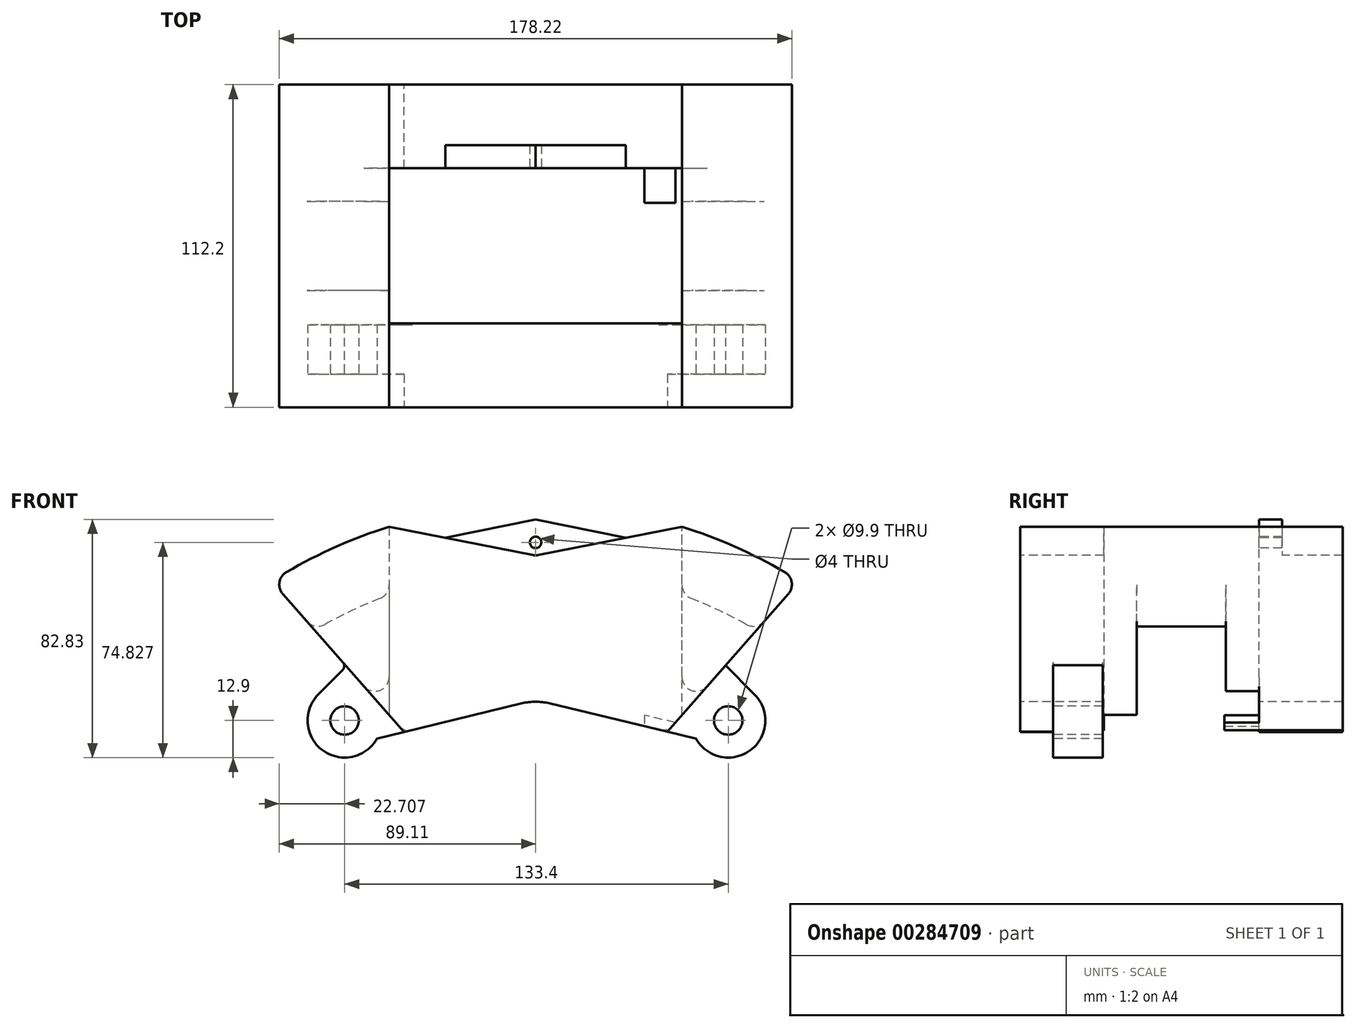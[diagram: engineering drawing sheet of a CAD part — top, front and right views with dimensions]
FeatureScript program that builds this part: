
annotation { "Feature Type Name" : "Feature", "Feature Type Description" : "" }
export const myFeature = defineFeature(function(context is Context, id is Id, definition is map)
    precondition{}
    {
        {
            var Q0;
            Q0=qCreatedBy(makeId("Front.planeOp"),FACE);
            var sketch = newSketch(context, id + "F0", { "sketchPlane" : qUnion([Q0])});
            skCircle(sketch, "E0", {"center": v(0, 0) * mm, "radius": 117.6 * mm, "construction": true});
            skPoint(sketch, "E1", {"position": v(67, 96.65) * mm});
            skLineSegment(sketch, "E2", {"start": v(67, 96.65) * mm, "end": v(-66.4, 96.65) * mm});
            skCircle(sketch, "E3", {"center": v(0, 0) * mm, "radius": 171.7 * mm, "construction": true});
            skCircle(sketch, "E4", {"center": v(67, 96.65) * mm, "radius": 4.95 * mm});
            skCircle(sketch, "E5", {"center": v(-66.4, 96.65) * mm, "radius": 4.95 * mm});
            skCircle(sketch, "E6", {"center": v(67, 96.65) * mm, "radius": 12.9 * mm});
            skCircle(sketch, "E7", {"center": v(-66.4, 96.65) * mm, "radius": 12.9 * mm});
            skPoint(sketch, "E8", {"position": v(-66.4, 83.75) * mm});
            skPoint(sketch, "E9", {"position": v(0, 83.75) * mm});
            skPoint(sketch, "E10", {"position": v(0, 103.75) * mm});
            skPoint(sketch, "E11", {"position": v(67, 83.75) * mm});
            skArc(sketch, "E12", {"start": v(55.76, 90.32) * mm, "mid": v(0.3, 103.75) * mm, "end": v(-55.16, 90.32) * mm});
            skPoint(sketch, "E13", {"position": v(0, 171.7) * mm});
            skPoint(sketch, "E14", {"position": v(91.53, 171.7) * mm});
            skLineSegment(sketch, "E15", {"start": v(-87.87, 140.62) * mm, "end": v(-67.03, 116.9) * mm});
            skPoint(sketch, "E16", {"position": v(-79.3, 96.65) * mm});
            skLineSegment(sketch, "E17", {"start": v(-66.4, 96.65) * mm, "end": v(-79.3, 96.65) * mm, "construction": true});
            skLineSegment(sketch, "E18", {"start": v(-66.4, 96.65) * mm, "end": v(-75.53, 105.77) * mm, "construction": true});
            skLineSegment(sketch, "E19", {"start": v(-75.53, 105.77) * mm, "end": v(-67.12, 114.18) * mm});
            skLineSegment(sketch, "E20", {"start": v(0, 103.75) * mm, "end": v(0, 0) * mm, "construction": true});
            skLineSegment(sketch, "E21.MirrorCS", {"start": v(87.87, 140.62) * mm, "end": v(66.07, 115.82) * mm});
            skArc(sketch, "E22", {"start": v(86.64, 148.24) * mm, "mid": v(0, 171.7) * mm, "end": v(-86.64, 148.24) * mm});
            skPoint(sketch, "E23.visualSharp", {"position": v(91.8, 145.1) * mm});
            skArc(sketch, "E23.filletArc", {"start": v(87.87, 140.62) * mm, "mid": v(89.05, 144.72) * mm, "end": v(86.64, 148.24) * mm});
            skPoint(sketch, "E24.visualSharp", {"position": v(-91.8, 145.1) * mm});
            skArc(sketch, "E24.filletArc", {"start": v(-86.64, 148.24) * mm, "mid": v(-89.05, 144.72) * mm, "end": v(-87.87, 140.62) * mm});
            skPoint(sketch, "E25", {"position": v(89.05, 144.72) * mm});
            skPoint(sketch, "E26", {"position": v(-89.05, 144.72) * mm});
            skPoint(sketch, "E27.visualSharp", {"position": v(65.8, 115.5) * mm});
            skPoint(sketch, "E28.visualSharp", {"position": v(-65.8, 115.5) * mm});
            skArc(sketch, "E28.filletArc", {"start": v(-67.12, 114.18) * mm, "mid": v(-66.54, 115.53) * mm, "end": v(-67.03, 116.9) * mm});
            skPoint(sketch, "E29", {"position": v(50.9, 171.7) * mm});
            skLineSegment(sketch, "E30", {"start": v(50.9, 171.7) * mm, "end": v(50.9, 163.98) * mm, "construction": true});
            skLineSegment(sketch, "E31", {"start": v(50.9, 171.7) * mm, "end": v(-50.9, 171.7) * mm, "construction": true});
            skLineSegment(sketch, "E32", {"start": v(-50.9, 171.7) * mm, "end": v(-50.9, 163.98) * mm, "construction": true});
            skPoint(sketch, "E33", {"position": v(0, 163.98) * mm});
            skPoint(sketch, "E34", {"position": v(0, 153.98) * mm});
            skLineSegment(sketch, "E35", {"start": v(-50.9, 163.98) * mm, "end": v(-0.96, 154.17) * mm});
            skLineSegment(sketch, "E36", {"start": v(0.96, 154.17) * mm, "end": v(50.9, 163.98) * mm});
            skArc(sketch, "E37.filletArc", {"start": v(-0.96, 154.17) * mm, "mid": v(0, 154.08) * mm, "end": v(0.96, 154.17) * mm});
            skLineSegment(sketch, "E38", {"start": v(-4.7, 102.6) * mm, "end": v(-55.16, 90.32) * mm});
            skLineSegment(sketch, "E39", {"start": v(4.7, 102.62) * mm, "end": v(55.76, 90.32) * mm});
            skArc(sketch, "E40.filletArc", {"start": v(4.7, 102.62) * mm, "mid": v(0, 103.17) * mm, "end": v(-4.7, 102.6) * mm});
            skLineSegment(sketch, "E41", {"start": v(67, 96.65) * mm, "end": v(79.9, 96.65) * mm, "construction": true});
            skLineSegment(sketch, "E42", {"start": v(67, 96.65) * mm, "end": v(76.12, 105.77) * mm, "construction": true});
            skLineSegment(sketch, "E43", {"start": v(76.12, 105.77) * mm, "end": v(66.07, 115.82) * mm});
            skPoint(sketch, "E44.orphan", {"position": v(64.77, 114.33) * mm});
            skSolve(sketch);
        }
        {
            var Q0;
            {var subQ0=sQuery(id+"F0.wireOp",EDGE,"E12");var subQ1=sQuery(id+"F0.wireOp",EDGE,"E2");var subQ2=makeQuery(id+"F0.imprint","INTERSECT",VERTEX,{"disambiguationData":[OD(0.0)],"derivedFrom":[subQ1,subQ0]});Q0=makeQuery(id+"F0.imprint","IMPRINT",FACE,{"disambiguationData":[TD([[makeQuery(id+"F0.imprint","IMPRINT",EDGE,{"disambiguationData":[TD([[subQ2,1.0]])],"derivedFrom":subQ1}),1.0]])]});}
            var Q1;
            {var subQ0=sQuery(id+"F0.wireOp",EDGE,"E12");var subQ1=sQuery(id+"F0.wireOp",EDGE,"E2");var subQ2=makeQuery(id+"F0.imprint","INTERSECT",VERTEX,{"disambiguationData":[OD(1.0)],"derivedFrom":[subQ1,subQ0]});Q1=makeQuery(id+"F0.imprint","IMPRINT",FACE,{"disambiguationData":[TD([[makeQuery(id+"F0.imprint","IMPRINT",EDGE,{"disambiguationData":[TD([[subQ2,-1.0]])],"derivedFrom":subQ1}),1.0]])]});}
            var Q2;
            Q2=makeQuery(id+"F0.imprint","IMPRINT",FACE,{"disambiguationData":[TD([[makeQuery(id+"F0.imprint","IMPRINT",EDGE,{"derivedFrom":sQuery(id+"F0.wireOp",EDGE,"E4")}),-1.0]])]});
            var Q3;
            Q3=makeQuery(id+"F0.imprint","IMPRINT",FACE,{"disambiguationData":[TD([[makeQuery(id+"F0.imprint","IMPRINT",EDGE,{"derivedFrom":sQuery(id+"F0.wireOp",EDGE,"E5")}),-1.0]])]});
            var Q4;
            Q4=makeQuery(id+"F0.imprint","IMPRINT",FACE,{"disambiguationData":[TD([[makeQuery(id+"F0.imprint","IMPRINT",EDGE,{"derivedFrom":sQuery(id+"F0.wireOp",EDGE,"E15")}),1.0]])]});
            var Q5;
            {var subQ0=sQuery(id+"F0.wireOp",EDGE,"E40.filletArc");Q5=makeQuery(id+"F0.imprint","IMPRINT",FACE,{"disambiguationData":[TD([[makeQuery(id+"F0.imprint","IMPRINT",EDGE,{"derivedFrom":subQ0}),-1.0]])]});}
            var Q6;
            {var subQ0=sQuery(id+"F0.wireOp",EDGE,"E39");var subQ1=sQuery(id+"F0.wireOp",EDGE,"E2");var subQ2=makeQuery(id+"F0.imprint","INTERSECT",VERTEX,{"derivedFrom":[subQ1,subQ0]});Q6=makeQuery(id+"F0.imprint","IMPRINT",FACE,{"disambiguationData":[TD([[makeQuery(id+"F0.imprint","IMPRINT",EDGE,{"disambiguationData":[TD([[subQ2,1.0]])],"derivedFrom":subQ1}),1.0]])]});}
            var Q7;
            {var subQ0=sQuery(id+"F0.wireOp",EDGE,"E38");var subQ1=sQuery(id+"F0.wireOp",EDGE,"E2");var subQ2=makeQuery(id+"F0.imprint","INTERSECT",VERTEX,{"derivedFrom":[subQ1,subQ0]});Q7=makeQuery(id+"F0.imprint","IMPRINT",FACE,{"disambiguationData":[TD([[makeQuery(id+"F0.imprint","IMPRINT",EDGE,{"disambiguationData":[TD([[subQ2,-1.0]])],"derivedFrom":subQ1}),1.0]])]});}
            extrude(context, id + "F1", {"entities" : qUnion([Q0, Q1, Q2, Q3, Q4, Q5, Q6, Q7]), "oppositeDirection" : true, "depth" : 112.2 * mm});
        }
        {
            var Q0;
            Q0=qCreatedBy(makeId("Front.planeOp"),FACE);
            cPlane(context, id + "F2", {"entities" : qUnion([Q0]), "cplaneType" : CPlaneType.OFFSET, "offset" : 40.6 * mm, "oppositeDirection" : true, "width" : 150 * mm, "height" : 150 * mm});
        }
        {
            var Q0;
            Q0=qCreatedBy(id+"F2.planeOp",FACE);
            var sketch = newSketch(context, id + "F3", { "sketchPlane" : qUnion([Q0])});
            skCircle(sketch, "E45", {"center": v(0, 0) * mm, "radius": 149.25 * mm});
            skSolve(sketch);
        }
        {
            var Q0;
            Q0 = qSketchRegion(id + "F3", true);
            extrude(context, id + "F4", {"entities" : qUnion([Q0]), "operationType" : NewBodyOperationType.REMOVE, "oppositeDirection" : true, "depth" : 31 * mm});
        }
        {
            var Q0;
            Q0=qCreatedBy(makeId("Front.planeOp"),FACE);
            cPlane(context, id + "F5", {"entities" : qUnion([Q0]), "cplaneType" : CPlaneType.OFFSET, "offset" : 29.1 * mm, "oppositeDirection" : true, "width" : 150 * mm, "height" : 150 * mm});
        }
        {
            var Q0;
            Q0=qCreatedBy(id+"F5.planeOp",FACE);
            var sketch = newSketch(context, id + "F6", { "sketchPlane" : qUnion([Q0])});
            skCircle(sketch, "E46.0", {"center": v(-66.4, 96.65) * mm, "radius": 4.95 * mm, "construction": true});
            skPoint(sketch, "E47", {"position": v(0, 63) * mm});
            skLineSegment(sketch, "E48.bottom", {"start": v(0, 63) * mm, "end": v(50.9, 63) * mm});
            skLineSegment(sketch, "E48.top", {"start": v(0, 63) * mm, "end": v(50.9, 63) * mm});
            skLineSegment(sketch, "E48.left", {"start": v(0, 63) * mm, "end": v(0, 63) * mm});
            skLineSegment(sketch, "E48.right", {"start": v(50.9, 63) * mm, "end": v(50.9, 63) * mm});
            skLineSegment(sketch, "E49", {"start": v(50.9, 63) * mm, "end": v(50.9, 173) * mm});
            skLineSegment(sketch, "E50", {"start": v(50.9, 173) * mm, "end": v(-50.9, 173) * mm});
            skLineSegment(sketch, "E51", {"start": v(-50.9, 173) * mm, "end": v(-50.9, 63) * mm});
            skLineSegment(sketch, "E52", {"start": v(-50.9, 63) * mm, "end": v(0, 63) * mm});
            skSolve(sketch);
        }
        {
            var Q0;
            Q0 = qSketchRegion(id + "F6", true);
            extrude(context, id + "F7", {"entities" : qUnion([Q0]), "operationType" : NewBodyOperationType.REMOVE, "oppositeDirection" : true, "depth" : 54 * mm});
        }
        {
            var Q0;
            Q0=makeQuery(id+"F1.opExtrude","CAP_FACE",FACE,{"disambiguationData":[OSD([sQuery(id+"F0.wireOp",EDGE,"E4"),sQuery(id+"F0.wireOp",EDGE,"E5"),sQuery(id+"F0.wireOp",EDGE,"E6"),sQuery(id+"F0.wireOp",EDGE,"E7"),sQuery(id+"F0.wireOp",EDGE,"E12"),sQuery(id+"F0.wireOp",EDGE,"E15"),sQuery(id+"F0.wireOp",EDGE,"E19"),sQuery(id+"F0.wireOp",EDGE,"E21.MirrorCS"),sQuery(id+"F0.wireOp",EDGE,"1f8badd5-7baa-4620-a5a9-6ada6518be5f0.MirrorCS"),sQuery(id+"F0.wireOp",EDGE,"E22"),sQuery(id+"F0.wireOp",EDGE,"E23.filletArc"),sQuery(id+"F0.wireOp",EDGE,"E24.filletArc"),sQuery(id+"F0.wireOp",EDGE,"E27.filletArc"),sQuery(id+"F0.wireOp",EDGE,"E28.filletArc"),sQuery(id+"F0.wireOp",EDGE,"E35"),sQuery(id+"F0.wireOp",EDGE,"E36"),sQuery(id+"F0.wireOp",EDGE,"E37.filletArc")])],"isStart":false});
            var sketch = newSketch(context, id + "F8", { "sketchPlane" : qUnion([Q0])});
            skLineSegment(sketch, "E53.0", {"start": v(-87.87, 140.62) * mm, "end": v(-87.87, 140.62) * mm});
            skLineSegment(sketch, "E54.0", {"start": v(87.87, 140.62) * mm, "end": v(67.03, 116.9) * mm});
            skArc(sketch, "E55.0", {"start": v(75.53, 105.77) * mm, "mid": v(77.23, 89.63) * mm, "end": v(61.8, 84.6) * mm});
            skLineSegment(sketch, "E56.0", {"start": v(75.53, 105.77) * mm, "end": v(67.12, 114.18) * mm});
            skArc(sketch, "E57.0", {"start": v(67.12, 114.18) * mm, "mid": v(66.54, 115.53) * mm, "end": v(67.03, 116.9) * mm});
            skLineSegment(sketch, "E58.0", {"start": v(4.7, 102.6) * mm, "end": v(55.16, 90.32) * mm});
            skLineSegment(sketch, "E59.0", {"start": v(-4.7, 102.62) * mm, "end": v(-55.76, 90.32) * mm});
            skArc(sketch, "E60.0", {"start": v(-4.7, 102.62) * mm, "mid": v(0, 103.17) * mm, "end": v(4.7, 102.6) * mm});
            skLineSegment(sketch, "E61", {"start": v(-87.87, 140.62) * mm, "end": v(-45.78, 92.72) * mm});
            skLineSegment(sketch, "E62", {"start": v(67.03, 116.9) * mm, "end": v(45.7, 92.62) * mm});
            skLineSegment(sketch, "E63.0", {"start": v(-76.12, 105.77) * mm, "end": v(-66.07, 115.82) * mm});
            skArc(sketch, "E64.0", {"start": v(-55.76, 90.32) * mm, "mid": v(-74.8, 86.37) * mm, "end": v(-76.12, 105.77) * mm});
            skSolve(sketch);
        }
        {
            var Q0;
            {var subQ4=sQuery(id+"F8.wireOp",EDGE,"E55.0");Q0=makeQuery(id+"F8.imprint","IMPRINT",FACE,{"disambiguationData":[TD([[makeQuery(id+"F8.imprint","IMPRINT",EDGE,{"derivedFrom":subQ4}),-1.0]])]});}
            var Q1;
            {var subQ1=sQuery(id+"F8.wireOp",EDGE,"E63.0");Q1=makeQuery(id+"F8.imprint","IMPRINT",FACE,{"disambiguationData":[TD([[makeQuery(id+"F8.imprint","IMPRINT",EDGE,{"derivedFrom":subQ1}),-1.0]])]});}
            extrude(context, id + "F9", {"entities" : qUnion([Q0, Q1]), "operationType" : NewBodyOperationType.REMOVE, "oppositeDirection" : true, "depth" : 41 * mm});
        }
        {
            var Q0;
            Q0=makeQuery(id+"F1.opExtrude","CAP_FACE",FACE,{"disambiguationData":[OSD([sQuery(id+"F0.wireOp",EDGE,"E4"),sQuery(id+"F0.wireOp",EDGE,"E5"),sQuery(id+"F0.wireOp",EDGE,"E6"),sQuery(id+"F0.wireOp",EDGE,"E7"),sQuery(id+"F0.wireOp",EDGE,"E12"),sQuery(id+"F0.wireOp",EDGE,"E15"),sQuery(id+"F0.wireOp",EDGE,"E19"),sQuery(id+"F0.wireOp",EDGE,"E21.MirrorCS"),sQuery(id+"F0.wireOp",EDGE,"1f8badd5-7baa-4620-a5a9-6ada6518be5f0.MirrorCS"),sQuery(id+"F0.wireOp",EDGE,"E22"),sQuery(id+"F0.wireOp",EDGE,"E23.filletArc"),sQuery(id+"F0.wireOp",EDGE,"E24.filletArc"),sQuery(id+"F0.wireOp",EDGE,"E27.filletArc"),sQuery(id+"F0.wireOp",EDGE,"E28.filletArc"),sQuery(id+"F0.wireOp",EDGE,"E35"),sQuery(id+"F0.wireOp",EDGE,"E36"),sQuery(id+"F0.wireOp",EDGE,"E37.filletArc")])],"isStart":true});
            var sketch = newSketch(context, id + "F10", { "sketchPlane" : qUnion([Q0])});
            skLineSegment(sketch, "E65.0", {"start": v(-87.87, 140.62) * mm, "end": v(-67.03, 116.9) * mm});
            skLineSegment(sketch, "E66.0", {"start": v(87.87, 140.62) * mm, "end": v(87.87, 140.62) * mm});
            skArc(sketch, "E67.0", {"start": v(-67.12, 114.18) * mm, "mid": v(-66.54, 115.53) * mm, "end": v(-67.03, 116.9) * mm});
            skLineSegment(sketch, "E68.0", {"start": v(-75.53, 105.77) * mm, "end": v(-67.12, 114.18) * mm});
            skArc(sketch, "E69.0", {"start": v(-75.53, 105.77) * mm, "mid": v(-77.23, 89.63) * mm, "end": v(-61.8, 84.6) * mm});
            skArc(sketch, "E70.0", {"start": v(62, 84.76) * mm, "mid": v(77.7, 89.46) * mm, "end": v(76.12, 105.77) * mm});
            skLineSegment(sketch, "E71.0", {"start": v(4.7, 102.62) * mm, "end": v(55.76, 90.32) * mm});
            skLineSegment(sketch, "E72.0", {"start": v(-4.7, 102.6) * mm, "end": v(-55.16, 90.32) * mm});
            skArc(sketch, "E73.0", {"start": v(4.7, 102.62) * mm, "mid": v(0, 103.17) * mm, "end": v(-4.7, 102.6) * mm});
            skLineSegment(sketch, "E74", {"start": v(-67.03, 116.9) * mm, "end": v(-45.7, 92.62) * mm});
            skLineSegment(sketch, "E75", {"start": v(87.87, 140.62) * mm, "end": v(45.78, 92.72) * mm});
            skLineSegment(sketch, "E76.0", {"start": v(76.12, 105.77) * mm, "end": v(66.07, 115.82) * mm});
            skSolve(sketch);
        }
        {
            var Q0;
            Q0=makeQuery(id+"F10.imprint","IMPRINT",FACE,{"disambiguationData":[TD([[makeQuery(id+"F10.imprint","IMPRINT",EDGE,{"derivedFrom":sQuery(id+"F10.wireOp",EDGE,"E67.0")}),-1.0]])]});
            var Q1;
            {var subQ6=sQuery(id+"F10.wireOp",EDGE,"E70.0");Q1=makeQuery(id+"F10.imprint","IMPRINT",FACE,{"disambiguationData":[TD([[makeQuery(id+"F10.imprint","IMPRINT",EDGE,{"derivedFrom":subQ6}),1.0]])]});}
            extrude(context, id + "F11", {"entities" : qUnion([Q0, Q1]), "operationType" : NewBodyOperationType.REMOVE, "oppositeDirection" : true, "depth" : 11.5 * mm});
        }
        {
            var Q0;
            Q0=makeQuery(id+"F7.boolean.opBoolean","COPY",FACE,{"derivedFrom":makeQuery(id+"F7.opExtrude","CAP_FACE",FACE,{"disambiguationData":[OSD([sQuery(id+"F6.wireOp",EDGE,"E48.top"),sQuery(id+"F6.wireOp",EDGE,"E49"),sQuery(id+"F6.wireOp",EDGE,"E50"),sQuery(id+"F6.wireOp",EDGE,"E51"),sQuery(id+"F6.wireOp",EDGE,"E52")])],"isStart":false})});
            var sketch = newSketch(context, id + "F12", { "sketchPlane" : qUnion([Q0])});
            skArc(sketch, "E77.0", {"start": v(0.96, 154.17) * mm, "mid": v(0, 154.08) * mm, "end": v(-0.96, 154.17) * mm});
            skPoint(sketch, "E78", {"position": v(0, 166.58) * mm});
            skPoint(sketch, "E78.positionSnap0", {"position": v(0, 154.08) * mm});
            skPoint(sketch, "E79", {"position": v(31.42, 160.15) * mm});
            skPoint(sketch, "E80", {"position": v(-31.42, 160.15) * mm});
            skLineSegment(sketch, "E81", {"start": v(0, 166.58) * mm, "end": v(-31.42, 160.15) * mm});
            skLineSegment(sketch, "E82", {"start": v(0, 166.58) * mm, "end": v(31.42, 160.15) * mm});
            skPoint(sketch, "E83", {"position": v(0, 158.58) * mm});
            skCircle(sketch, "E84", {"center": v(0, 158.58) * mm, "radius": 2 * mm});
            skSolve(sketch);
        }
        {
            var Q0;
            {var subQ2=sQuery(id+"F12.wireOp",EDGE,"E77.0");Q0=makeQuery(id+"F12.imprint","IMPRINT",FACE,{"disambiguationData":[TD([[makeQuery(id+"F12.imprint","IMPRINT",EDGE,{"derivedFrom":subQ2}),-1.0]])]});}
            extrude(context, id + "F13", {"entities" : qUnion([Q0]), "operationType" : NewBodyOperationType.ADD, "oppositeDirection" : true, "depth" : 8 * mm});
        }
        {
            var Q0;
            Q0=qCreatedBy(makeId("Front.planeOp"),FACE);
            cPlane(context, id + "F14", {"entities" : qUnion([Q0]), "cplaneType" : CPlaneType.OFFSET, "offset" : 56.1 * mm, "oppositeDirection" : true, "width" : 150 * mm, "height" : 150 * mm});
        }
        {
            var Q0;
            Q0=makeQuery(id+"F9.boolean.opBoolean","INTERSECT",EDGE,{"derivedFrom":[makeQuery(id+"F7.boolean.opBoolean","COPY",FACE,{"derivedFrom":makeQuery(id+"F7.opExtrude","SWEPT_FACE",FACE,{"disambiguationData":[OSD([sQuery(id+"F6.wireOp",EDGE,"E49")])]})}),makeQuery(id+"F9.opExtrude","SWEPT_FACE",FACE,{"disambiguationData":[OSD([sQuery(id+"F8.wireOp",EDGE,"E61")])]})]});
            var Q1;
            Q1=makeQuery(id+"FAadXu5jNJjpnGG_1.boolean.opBoolean","INTERSECT",EDGE,{"derivedFrom":[makeQuery(id+"F7.boolean.opBoolean","COPY",FACE,{"derivedFrom":makeQuery(id+"F7.opExtrude","SWEPT_FACE",FACE,{"disambiguationData":[OSD([sQuery(id+"F6.wireOp",EDGE,"E49")])]})}),makeQuery(id+"FAadXu5jNJjpnGG_1.opExtrude","SWEPT_FACE",FACE,{"disambiguationData":[OSD([sQuery(id+"FpSLTYn3EKaI7YF_1.wireOp",EDGE,"21a007ec-3ae1-4423-a903-17e2e16a2fb4.0.1")])]})]});
            var Q2;
            Q2=makeQuery(id+"F9.boolean.opBoolean","INTERSECT",EDGE,{"derivedFrom":[makeQuery(id+"F7.boolean.opBoolean","COPY",FACE,{"derivedFrom":makeQuery(id+"F7.opExtrude","SWEPT_FACE",FACE,{"disambiguationData":[OSD([sQuery(id+"F6.wireOp",EDGE,"E51")])]})}),makeQuery(id+"F9.opExtrude","SWEPT_FACE",FACE,{"disambiguationData":[OSD([sQuery(id+"F8.wireOp",EDGE,"E62")])]})]});
            var Q3;
            Q3=makeQuery(id+"FAadXu5jNJjpnGG_1.boolean.opBoolean","INTERSECT",EDGE,{"derivedFrom":[makeQuery(id+"F7.boolean.opBoolean","COPY",FACE,{"derivedFrom":makeQuery(id+"F7.opExtrude","SWEPT_FACE",FACE,{"disambiguationData":[OSD([sQuery(id+"F6.wireOp",EDGE,"E51")])]})}),makeQuery(id+"FAadXu5jNJjpnGG_1.opExtrude","SWEPT_FACE",FACE,{"disambiguationData":[OSD([sQuery(id+"FpSLTYn3EKaI7YF_1.wireOp",EDGE,"04f76ab2-53ae-477f-a4d8-78d7091b372c.0.0")])]})]});
            var Q4;
            {var subQ1=sQuery(id+"F0.wireOp",EDGE,"E39");Q4=makeQuery(id+"FAadXu5jNJjpnGG_1.boolean.opBoolean","MERGE",EDGE,{"derivedFrom":[makeQuery(id+"F7.boolean.opBoolean","INTERSECT",EDGE,{"derivedFrom":[makeQuery(id+"F4.boolean.opBoolean","SPLIT",FACE,{"disambiguationData":[TD([makeQuery(id+"F4.opExtrude","CAP_FACE",FACE,{"disambiguationData":[OSD([sQuery(id+"F3.wireOp",EDGE,"E45")])],"isStart":true})])],"derivedFrom":makeQuery(id+"F1.opExtrude","SWEPT_FACE",FACE,{"disambiguationData":[OSD([subQ1])]})}),makeQuery(id+"F7.opExtrude","SWEPT_FACE",FACE,{"disambiguationData":[OSD([sQuery(id+"F6.wireOp",EDGE,"E49")])]})]}),makeQuery(id+"FAadXu5jNJjpnGG_1.opExtrude","SWEPT_EDGE",EDGE,{"disambiguationData":[OSD([sQuery(id+"FpSLTYn3EKaI7YF_1.wireOp",EDGE,"68c81afa-a9c1-4998-8d95-a05e8360465f.0.0"),sQuery(id+"FpSLTYn3EKaI7YF_1.wireOp",EDGE,"cEKWUgf6-4L0R-zaLr-fLBW-bOH0qmf5rE12")])]})]});}
            fillet(context, id + "F15", {"entities" : qUnion([Q0, Q1, Q2, Q3, Q4]), "radius" : 5 * mm, "tangentPropagation" : true, "allowEdgeOverflow" : false});
        }
        {
            var Q0;
            {var subQ0=sQuery(id+"F6.wireOp",EDGE,"E52");var subQ1=sQuery(id+"F6.wireOp",EDGE,"E51");var subQ2=sQuery(id+"F6.wireOp",EDGE,"E50");var subQ3=sQuery(id+"F6.wireOp",EDGE,"E49");var subQ4=sQuery(id+"F6.wireOp",EDGE,"E48.top");Q0=makeQuery(id+"F13.boolean.opBoolean","MERGE",FACE,{"derivedFrom":[makeQuery(id+"F7.boolean.opBoolean","COPY",FACE,{"derivedFrom":makeQuery(id+"F7.opExtrude","CAP_FACE",FACE,{"disambiguationData":[OSD([subQ4,subQ3,subQ2,subQ1,subQ0])],"isStart":false})}),makeQuery(id+"F13.opExtrude","CAP_FACE",FACE,{"disambiguationData":[OSD([sQuery(id+"F0.wireOp",EDGE,"E35"),sQuery(id+"F0.wireOp",EDGE,"E36"),subQ4,subQ3,subQ2,subQ1,subQ0,sQuery(id+"F12.wireOp",EDGE,"E77.0"),sQuery(id+"F12.wireOp",EDGE,"E81"),sQuery(id+"F12.wireOp",EDGE,"E82"),sQuery(id+"F12.wireOp",EDGE,"E84")])],"isStart":true})]});}
            var sketch = newSketch(context, id + "F16", { "sketchPlane" : qUnion([Q0])});
            skLineSegment(sketch, "E85.0", {"start": v(45.78, 92.72) * mm, "end": v(48.6, 95.93) * mm});
            skPoint(sketch, "E86", {"position": v(41.49, 87.84) * mm});
            skLineSegment(sketch, "E87.0", {"start": v(45.78, 92.72) * mm, "end": v(37.9, 94.62) * mm});
            skPoint(sketch, "E88.newPointB", {"position": v(4.7, 102.62) * mm});
            skLineSegment(sketch, "E89", {"start": v(48.6, 95.93) * mm, "end": v(37.9, 98.5) * mm});
            skLineSegment(sketch, "E90", {"start": v(37.9, 98.5) * mm, "end": v(37.9, 94.62) * mm});
            skSolve(sketch);
        }
        {
            var Q0;
            Q0=makeQuery(id+"F16.imprint","IMPRINT",FACE,{"disambiguationData":[TD([[makeQuery(id+"F16.imprint","IMPRINT",EDGE,{"derivedFrom":sQuery(id+"F16.wireOp",EDGE,"E85.0")}),1.0]])]});
            extrude(context, id + "F17", {"entities" : qUnion([Q0]), "operationType" : NewBodyOperationType.ADD, "depth" : 12 * mm});
        }
        {
            var Q0;
            Q0=makeQuery(id+"F11.boolean.opBoolean","COPY",EDGE,{"derivedFrom":makeQuery(id+"F11.opExtrude","SWEPT_EDGE",EDGE,{"disambiguationData":[OSD([sQuery(id+"F10.wireOp",EDGE,"E72.0"),sQuery(id+"F10.wireOp",EDGE,"E74")])]})});
            var Q1;
            Q1=makeQuery(id+"F11.boolean.opBoolean","COPY",EDGE,{"derivedFrom":makeQuery(id+"F11.opExtrude","SWEPT_EDGE",EDGE,{"disambiguationData":[OSD([sQuery(id+"F10.wireOp",EDGE,"E71.0"),sQuery(id+"F10.wireOp",EDGE,"E75")])]})});
            var Q2;
            Q2=makeQuery(id+"F17.boolean.opBoolean","MERGE",EDGE,{"derivedFrom":[makeQuery(id+"F9.boolean.opBoolean","COPY",EDGE,{"derivedFrom":makeQuery(id+"F9.opExtrude","SWEPT_EDGE",EDGE,{"disambiguationData":[OSD([sQuery(id+"F8.wireOp",EDGE,"E59.0"),sQuery(id+"F8.wireOp",EDGE,"E61")])]})}),makeQuery(id+"F17.opExtrude","SWEPT_EDGE",EDGE,{"disambiguationData":[OSD([sQuery(id+"F16.wireOp",EDGE,"E85.0"),sQuery(id+"F16.wireOp",EDGE,"E87.0")])]})]});
            var Q3;
            Q3=makeQuery(id+"F9.boolean.opBoolean","COPY",EDGE,{"derivedFrom":makeQuery(id+"F9.opExtrude","SWEPT_EDGE",EDGE,{"disambiguationData":[OSD([sQuery(id+"F8.wireOp",EDGE,"E58.0"),sQuery(id+"F8.wireOp",EDGE,"E62")])]})});
            fillet(context, id + "F18", {"entities" : qUnion([Q0, Q1, Q2, Q3]), "radius" : 5 * mm, "tangentPropagation" : true, "allowEdgeOverflow" : false});
        }
        {
            var Q0;
            Q0=makeQuery(id+"F4.boolean.opBoolean","INTERSECT",EDGE,{"derivedFrom":[makeQuery(id+"F1.opExtrude","SWEPT_FACE",FACE,{"disambiguationData":[OSD([sQuery(id+"F0.wireOp",EDGE,"E15")])]}),makeQuery(id+"F4.opExtrude","SWEPT_FACE",FACE,{"disambiguationData":[OSD([sQuery(id+"F3.wireOp",EDGE,"E45")])]})]});
            var Q1;
            Q1=makeQuery(id+"F7.boolean.opBoolean","INTERSECT",EDGE,{"derivedFrom":[makeQuery(id+"F4.boolean.opBoolean","COPY",FACE,{"derivedFrom":makeQuery(id+"F4.opExtrude","SWEPT_FACE",FACE,{"disambiguationData":[OSD([sQuery(id+"F3.wireOp",EDGE,"E45")])]})}),makeQuery(id+"F7.opExtrude","SWEPT_FACE",FACE,{"disambiguationData":[OSD([sQuery(id+"F6.wireOp",EDGE,"E51")])]})]});
            var Q2;
            Q2=makeQuery(id+"F4.boolean.opBoolean","INTERSECT",EDGE,{"derivedFrom":[makeQuery(id+"F1.opExtrude","SWEPT_FACE",FACE,{"disambiguationData":[OSD([sQuery(id+"F0.wireOp",EDGE,"E21.MirrorCS")])]}),makeQuery(id+"F4.opExtrude","SWEPT_FACE",FACE,{"disambiguationData":[OSD([sQuery(id+"F3.wireOp",EDGE,"E45")])]})]});
            var Q3;
            Q3=makeQuery(id+"F7.boolean.opBoolean","INTERSECT",EDGE,{"derivedFrom":[makeQuery(id+"F4.boolean.opBoolean","COPY",FACE,{"derivedFrom":makeQuery(id+"F4.opExtrude","SWEPT_FACE",FACE,{"disambiguationData":[OSD([sQuery(id+"F3.wireOp",EDGE,"E45")])]})}),makeQuery(id+"F7.opExtrude","SWEPT_FACE",FACE,{"disambiguationData":[OSD([sQuery(id+"F6.wireOp",EDGE,"E49")])]})]});
            fillet(context, id + "F19", {"entities" : qUnion([Q0, Q1, Q2, Q3]), "radius" : 5 * mm, "tangentPropagation" : true, "allowEdgeOverflow" : false});
        }
        {
            var Q0;
            Q0=makeQuery(id+"F11.boolean.opBoolean","COPY",FACE,{"derivedFrom":makeQuery(id+"F11.opExtrude","CAP_FACE",FACE,{"disambiguationData":[OSD([sQuery(id+"F0.wireOp",EDGE,"E5"),sQuery(id+"F0.wireOp",EDGE,"E7"),sQuery(id+"F10.wireOp",EDGE,"E67.0"),sQuery(id+"F10.wireOp",EDGE,"E68.0"),sQuery(id+"F10.wireOp",EDGE,"E69.0"),sQuery(id+"F10.wireOp",EDGE,"E72.0"),sQuery(id+"F10.wireOp",EDGE,"E74")])],"isStart":false})});
            cPlane(context, id + "F20", {"entities" : qUnion([Q0]), "cplaneType" : CPlaneType.OFFSET, "offset" : 17.2 * mm, "oppositeDirection" : true, "width" : 150 * mm, "height" : 150 * mm});
        }
        {
            var Q0;
            Q0=qCreatedBy(id+"F20.planeOp",FACE);
            var sketch = newSketch(context, id + "F21", { "sketchPlane" : qUnion([Q0])});
            skLineSegment(sketch, "E91.0.0", {"start": v(-47.7, 94.9) * mm, "end": v(-67.03, 116.9) * mm});
            skArc(sketch, "E91.0.1", {"start": v(-67.03, 116.9) * mm, "mid": v(-66.54, 115.53) * mm, "end": v(-67.12, 114.18) * mm});
            skLineSegment(sketch, "E91.0.2", {"start": v(-67.12, 114.18) * mm, "end": v(-75.53, 105.77) * mm});
            skArc(sketch, "E91.0.3", {"start": v(-75.53, 105.77) * mm, "mid": v(-74.2, 86.37) * mm, "end": v(-55.16, 90.32) * mm});
            skLineSegment(sketch, "E91.0.4", {"start": v(-55.16, 90.32) * mm, "end": v(-42.75, 93.34) * mm});
            skArc(sketch, "E91.0.5", {"start": v(-42.75, 93.34) * mm, "mid": v(-45.44, 93.43) * mm, "end": v(-47.7, 94.9) * mm});
            skLineSegment(sketch, "E92.0.0", {"start": v(76.12, 105.77) * mm, "end": v(66.07, 115.82) * mm});
            skLineSegment(sketch, "E92.0.1", {"start": v(66.07, 115.82) * mm, "end": v(47.77, 95) * mm});
            skArc(sketch, "E92.0.2", {"start": v(47.77, 95) * mm, "mid": v(45.53, 93.52) * mm, "end": v(42.85, 93.43) * mm});
            skLineSegment(sketch, "E92.0.3", {"start": v(42.85, 93.43) * mm, "end": v(55.76, 90.32) * mm});
            skArc(sketch, "E92.0.4", {"start": v(55.76, 90.32) * mm, "mid": v(74.8, 86.37) * mm, "end": v(76.12, 105.77) * mm});
            skSolve(sketch);
        }
        {
            var Q0;
            Q0=makeQuery(id+"F21.imprint","IMPRINT",FACE,{"disambiguationData":[TD([[makeQuery(id+"F21.imprint","IMPRINT",EDGE,{"derivedFrom":sQuery(id+"F21.wireOp",EDGE,"E91.0.0")}),1.0]])]});
            var Q1;
            Q1=makeQuery(id+"F21.imprint","IMPRINT",FACE,{"disambiguationData":[TD([[makeQuery(id+"F21.imprint","IMPRINT",EDGE,{"derivedFrom":sQuery(id+"F21.wireOp",EDGE,"E92.0.0")}),1.0]])]});
            extrude(context, id + "F22", {"entities" : qUnion([Q0, Q1]), "operationType" : NewBodyOperationType.REMOVE, "oppositeDirection" : true, "depth" : 25 * mm});
        }
    });
